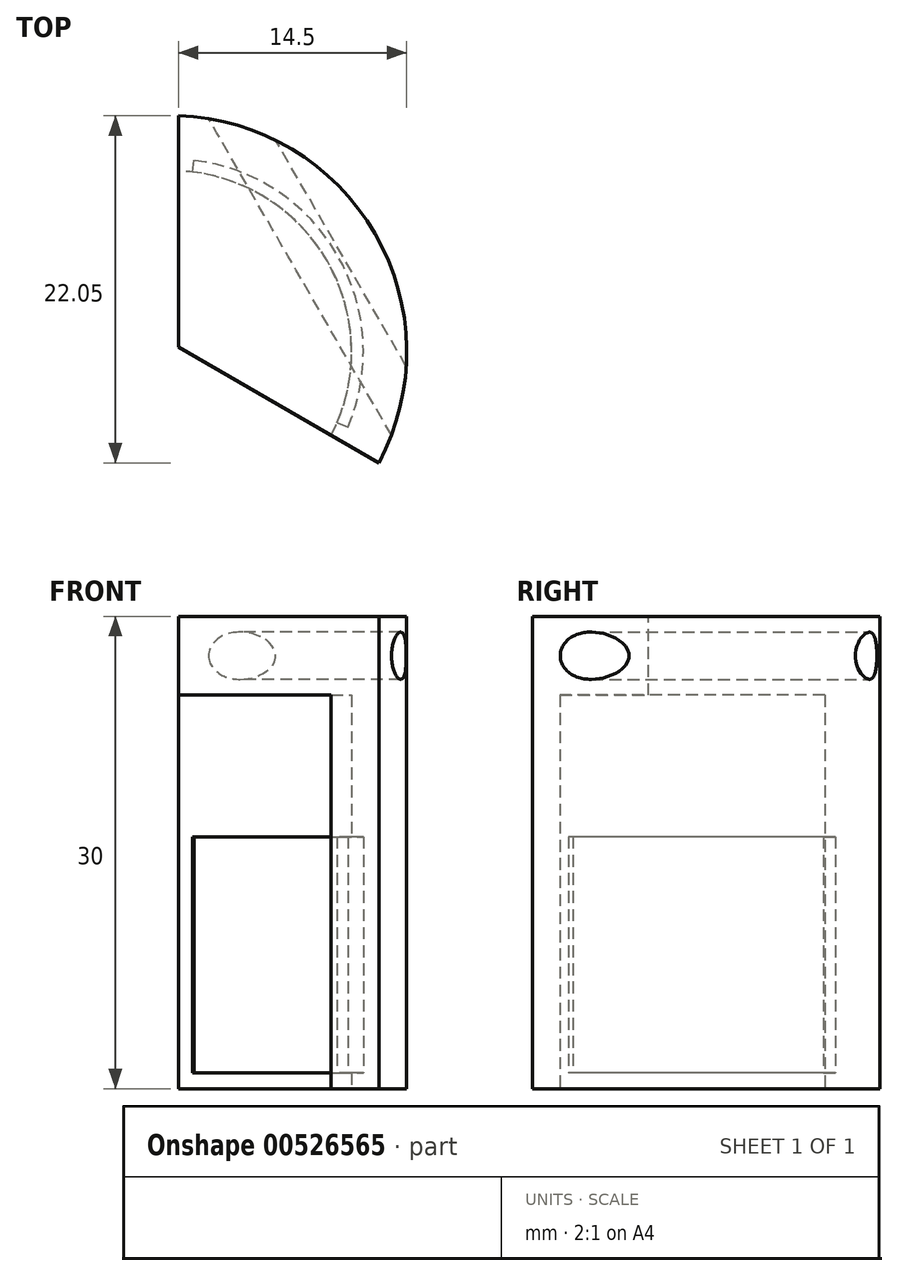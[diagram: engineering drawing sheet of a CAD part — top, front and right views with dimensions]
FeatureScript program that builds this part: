
annotation { "Feature Type Name" : "Feature", "Feature Type Description" : "" }
export const myFeature = defineFeature(function(context is Context, id is Id, definition is map)
    precondition{}
    {
        {
            var Q0;
            Q0=qCreatedBy(makeId("Top.planeOp"),FACE);
            var sketch = newSketch(context, id + "F0", { "sketchPlane" : qUnion([Q0])});
            skArc(sketch, "E0", {"start": v(13, -7.5) * mm, "mid": v(13, 7.5) * mm, "end": v(0, 15) * mm});
            skLineSegment(sketch, "E1", {"start": v(0, 0) * mm, "end": v(0, 15) * mm});
            skLineSegment(sketch, "E2", {"start": v(0, 0) * mm, "end": v(13, -7.5) * mm});
            skSolve(sketch);
        }
        {
            var Q0;
            Q0=makeQuery(id+"F0.imprint","IMPRINT",FACE,{"disambiguationData":[TD([[makeQuery(id+"F0.imprint","IMPRINT",EDGE,{"derivedFrom":sQuery(id+"F0.wireOp",EDGE,"E0")}),1.0]])]});
            extrude(context, id + "F1", {"entities" : qUnion([Q0]), "oppositeDirection" : true, "depth" : 30 * mm, "offsetDistance" : 25 * mm});
        }
        {
            var Q0;
            Q0=makeQuery(id+"F1.opExtrude","CAP_FACE",FACE,{"disambiguationData":[OSD([sQuery(id+"F0.wireOp",EDGE,"E0")])],"isStart":false});
            var sketch = newSketch(context, id + "F2", { "sketchPlane" : qUnion([Q0])});
            skCircle(sketch, "E3", {"center": v(0, 0) * mm, "radius": 11.5 * mm});
            skSolve(sketch);
        }
        {
            var Q0;
            Q0=makeQuery(id+"F2.imprint","IMPRINT",FACE,{"disambiguationData":[TD([[makeQuery(id+"F2.imprint","IMPRINT",EDGE,{"derivedFrom":sQuery(id+"F2.wireOp",EDGE,"E3")}),1.0]])]});
            extrude(context, id + "F3", {"entities" : qUnion([Q0]), "operationType" : NewBodyOperationType.REMOVE, "oppositeDirection" : true, "depth" : 25 * mm, "offsetDistance" : 25 * mm});
        }
        {
            var Q0;
            Q0=makeQuery(id+"F1.opExtrude","SWEPT_FACE",FACE,{"disambiguationData":[OSD([sQuery(id+"F0.wireOp",EDGE,"E1")])]});
            var Q1;
            Q1=makeQuery(id+"F1.opExtrude","SWEPT_EDGE",EDGE,{"disambiguationData":[OSD([sQuery(id+"F0.wireOp",EDGE,"E1"),sQuery(id+"F0.wireOp",EDGE,"E2")])]});
            cPlane(context, id + "F4", {"entities" : qUnion([Q0, Q1]), "cplaneType" : CPlaneType.LINE_ANGLE, "offset" : 25 * mm, "angle" : 60 * degree, "oppositeDirection" : true, "width" : 150 * mm, "height" : 150 * mm});
        }
        {
            var Q0;
            Q0=qCreatedBy(id+"F4.planeOp",FACE);
            var sketch = newSketch(context, id + "F5", { "sketchPlane" : qUnion([Q0])});
            skCircle(sketch, "E4", {"center": v(11, -2.5) * mm, "radius": 1.5 * mm});
            skSolve(sketch);
        }
        {
            var Q0;
            Q0 = qSketchRegion(id + "F5", true);
            extrude(context, id + "F6", {"entities" : qUnion([Q0]), "operationType" : NewBodyOperationType.REMOVE, "endBound" : BoundingType.SYMMETRIC, "depth" : 27 * mm, "offsetDistance" : 25 * mm});
        }
        {
            var Q0;
            Q0=makeQuery(id+"F1.opExtrude","CAP_FACE",FACE,{"disambiguationData":[OSD([sQuery(id+"F0.wireOp",EDGE,"E0"),sQuery(id+"F0.wireOp",EDGE,"E1"),sQuery(id+"F0.wireOp",EDGE,"E2")])],"isStart":true});
            var sketch = newSketch(context, id + "F7", { "sketchPlane" : qUnion([Q0])});
            skLineSegment(sketch, "E5", {"start": v(0.5, 0.29) * mm, "end": v(0.5, 16.41) * mm});
            skLineSegment(sketch, "E6", {"start": v(0.5, 0.29) * mm, "end": v(14, -7.51) * mm});
            skLineSegment(sketch, "E7", {"start": v(0.5, 16.41) * mm, "end": v(-0.91, 16.41) * mm});
            skLineSegment(sketch, "E8", {"start": v(-0.91, 16.41) * mm, "end": v(-0.91, -10.83) * mm});
            skLineSegment(sketch, "E9", {"start": v(-0.91, -10.83) * mm, "end": v(14, -10.83) * mm});
            skLineSegment(sketch, "E10", {"start": v(14, -10.83) * mm, "end": v(14, -7.51) * mm});
            skSolve(sketch);
        }
        {
            var Q0;
            {var subQ0=sQuery(id+"F7.wireOp",EDGE,"E7");Q0=makeQuery(id+"F7.imprint","IMPRINT",FACE,{"disambiguationData":[TD([[makeQuery(id+"F7.imprint","IMPRINT",EDGE,{"derivedFrom":subQ0}),1.0]])]});}
            var Q1;
            {var subQ1=makeQuery(id+"F1.opExtrude","CAP_EDGE",EDGE,{"disambiguationData":[OSD([sQuery(id+"F0.wireOp",EDGE,"E1")])],"isStart":true});Q1=makeQuery(id+"F7.imprint","IMPRINT",FACE,{"disambiguationData":[TD([[makeQuery(id+"F7.imprint","IMPRINT",EDGE,{"derivedFrom":subQ1}),-1.0]])]});}
            extrude(context, id + "F8", {"entities" : qUnion([Q0, Q1]), "operationType" : NewBodyOperationType.REMOVE, "oppositeDirection" : true, "depth" : 30 * mm, "offsetDistance" : 25 * mm});
        }
        {
            var Q0;
            Q0=makeQuery(id+"F1.opExtrude","CAP_FACE",FACE,{"disambiguationData":[OSD([sQuery(id+"F0.wireOp",EDGE,"E0"),sQuery(id+"F0.wireOp",EDGE,"E1"),sQuery(id+"F0.wireOp",EDGE,"E2")])],"isStart":false});
            cPlane(context, id + "F9", {"entities" : qUnion([Q0]), "cplaneType" : CPlaneType.OFFSET, "offset" : 1 * mm, "oppositeDirection" : true, "width" : 150 * mm, "height" : 150 * mm});
        }
        {
            var Q0;
            Q0=qCreatedBy(id+"F9.planeOp",FACE);
            var sketch = newSketch(context, id + "F10", { "sketchPlane" : qUnion([Q0])});
            skArc(sketch, "E11", {"start": v(1.22, -9.93) * mm, "mid": v(8.66, -5) * mm, "end": v(9.2, 3.9) * mm});
            skArc(sketch, "E12", {"start": v(1.5, -12.16) * mm, "mid": v(10.6, -6.13) * mm, "end": v(11.28, 4.79) * mm});
            skLineSegment(sketch, "E13", {"start": v(1.22, -9.93) * mm, "end": v(1.5, -12.16) * mm});
            skLineSegment(sketch, "E14", {"start": v(9.2, 3.9) * mm, "end": v(11.28, 4.79) * mm});
            skSolve(sketch);
        }
        {
            var Q0;
            Q0=makeQuery(id+"F10.imprint","IMPRINT",FACE,{"disambiguationData":[TD([[makeQuery(id+"F10.imprint","IMPRINT",EDGE,{"derivedFrom":sQuery(id+"F10.wireOp",EDGE,"E11")}),-1.0]])]});
            extrude(context, id + "F11", {"entities" : qUnion([Q0]), "operationType" : NewBodyOperationType.REMOVE, "oppositeDirection" : true, "depth" : 15 * mm, "offsetDistance" : 25 * mm});
        }
    });
